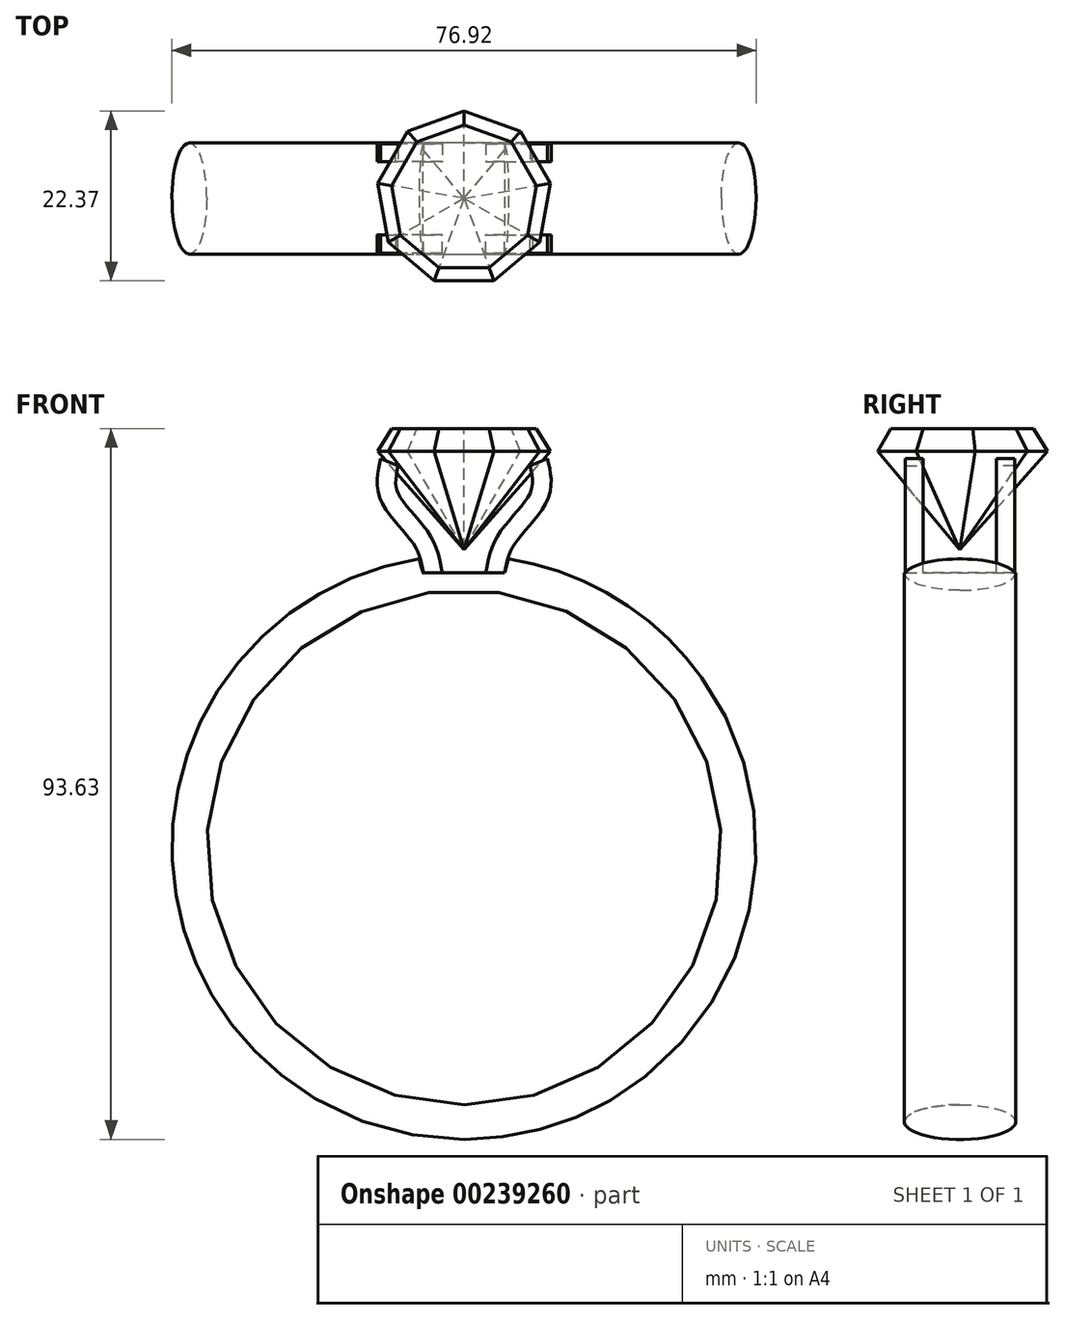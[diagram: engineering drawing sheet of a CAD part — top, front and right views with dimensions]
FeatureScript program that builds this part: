
annotation { "Feature Type Name" : "Feature", "Feature Type Description" : "" }
export const myFeature = defineFeature(function(context is Context, id is Id, definition is map)
    precondition{}
    {
        {
            var Q0;
            Q0=qCreatedBy(makeId("Right.planeOp"),FACE);
            var sketch = newSketch(context, id + "F0", { "sketchPlane" : qUnion([Q0])});
            skEllipse(sketch, "E0", {"center": v(0, 36.17) * mm, "majorRadius": 7.32 * mm, "minorRadius": 2.3 * mm, "majorAxis": v(1, 0)});
            skSolve(sketch);
        }
        {
            var Q0;
            Q0=qCreatedBy(makeId("Right.planeOp"),FACE);
            var sketch = newSketch(context, id + "F1", { "sketchPlane" : qUnion([Q0])});
            skLineSegment(sketch, "E1", {"start": v(-23.7, 0) * mm, "end": v(21.26, 0) * mm});
            skSolve(sketch);
        }
        {
            var Q0;
            Q0=makeQuery(id+"F0.imprint","IMPRINT",FACE,{"disambiguationData":[TD([[makeQuery(id+"F0.imprint","IMPRINT",EDGE,{"derivedFrom":sQuery(id+"F0.wireOp",EDGE,"E0")}),1.0]])]});
            var Q1;
            Q1=sQuery(id+"F0.wireOp",EDGE,"E0");
            var Q2;
            Q2=sQuery(id+"F1.wireOp",EDGE,"E1");
            revolve(context, id + "F2", {"entities" : qUnion([Q0]), "surfaceEntities" : qUnion([Q1]), "axis" : qUnion([Q2]), "revolveType" : RevolveType.FULL});
        }
        {
            var Q0;
            Q0=qCreatedBy(makeId("Top.planeOp"),FACE);
            var Q1;
            Q1=sQuery(id+"F0.wireOp",VERTEX,"E0.center");
            cPlane(context, id + "F3", {"entities" : qUnion([Q0, Q1]), "cplaneType" : CPlaneType.PLANE_POINT, "offset" : 100 * mm, "width" : 150 * mm, "height" : 150 * mm});
        }
        {
            var Q0;
            Q0=qCreatedBy(id+"F3.planeOp",FACE);
            var sketch = newSketch(context, id + "F4", { "sketchPlane" : qUnion([Q0])});
            skLineSegment(sketch, "E2.bottom", {"start": v(-5.43, 10.42) * mm, "end": v(5.35, 10.42) * mm});
            skLineSegment(sketch, "E2.top", {"start": v(-5.43, -11.19) * mm, "end": v(5.35, -11.19) * mm});
            skLineSegment(sketch, "E2.left", {"start": v(-5.43, 10.42) * mm, "end": v(-5.43, -11.19) * mm});
            skLineSegment(sketch, "E2.right", {"start": v(5.35, 10.42) * mm, "end": v(5.35, -11.19) * mm});
            skSolve(sketch);
        }
        {
            var Q0;
            Q0 = qSketchRegion(id + "F4", true);
            extrude(context, id + "F5", {"entities" : qUnion([Q0]), "operationType" : NewBodyOperationType.REMOVE, "depth" : 5.6 * mm, "hasDraft" : true, "draftAngle" : 15 * degree});
        }
        {
            var Q0;
            Q0=qCreatedBy(id+"F3.planeOp",FACE);
            cPlane(context, id + "F6", {"entities" : qUnion([Q0]), "cplaneType" : CPlaneType.OFFSET, "offset" : 19 * mm, "width" : 150 * mm, "height" : 150 * mm});
        }
        {
            var Q0;
            Q0=qCreatedBy(id+"F6.planeOp",FACE);
            var sketch = newSketch(context, id + "F7", { "sketchPlane" : qUnion([Q0])});
            skCircle(sketch, "E3.cCircle", {"center": v(0, 0) * mm, "radius": 9.1 * mm, "construction": true});
            skLineSegment(sketch, "E3.0", {"start": v(3.31, -9.1) * mm, "end": v(-3.31, -9.1) * mm});
            skLineSegment(sketch, "E3.1", {"start": v(-3.31, -9.1) * mm, "end": v(-8.4, -4.84) * mm});
            skLineSegment(sketch, "E3.2", {"start": v(-8.4, -4.84) * mm, "end": v(-9.54, 1.68) * mm});
            skLineSegment(sketch, "E3.3", {"start": v(-9.54, 1.68) * mm, "end": v(-6.23, 7.42) * mm});
            skLineSegment(sketch, "E3.4", {"start": v(-6.23, 7.42) * mm, "end": v(0, 9.69) * mm});
            skLineSegment(sketch, "E3.5", {"start": v(0, 9.69) * mm, "end": v(6.23, 7.42) * mm});
            skLineSegment(sketch, "E3.6", {"start": v(6.23, 7.42) * mm, "end": v(9.54, 1.68) * mm});
            skLineSegment(sketch, "E3.7", {"start": v(9.54, 1.68) * mm, "end": v(8.4, -4.84) * mm});
            skLineSegment(sketch, "E3.8", {"start": v(8.4, -4.84) * mm, "end": v(3.31, -9.1) * mm});
            skPoint(sketch, "E3.0.midPoint", {"position": v(0, -9.1) * mm});
            skSolve(sketch);
        }
        {
            var Q0;
            Q0 = qSketchRegion(id + "F7", true);
            extrude(context, id + "F8", {"entities" : qUnion([Q0]), "oppositeDirection" : true, "depth" : 3 * mm, "hasDraft" : true, "draftAngle" : 30 * degree});
        }
        {
            var Q0;
            Q0=makeQuery(id+"F8.opExtrude","CAP_FACE",FACE,{"disambiguationData":[OSD([sQuery(id+"F7.wireOp",EDGE,"E3.0"),sQuery(id+"F7.wireOp",EDGE,"E3.1"),sQuery(id+"F7.wireOp",EDGE,"E3.2"),sQuery(id+"F7.wireOp",EDGE,"E3.3"),sQuery(id+"F7.wireOp",EDGE,"E3.4"),sQuery(id+"F7.wireOp",EDGE,"E3.5"),sQuery(id+"F7.wireOp",EDGE,"E3.6"),sQuery(id+"F7.wireOp",EDGE,"E3.7"),sQuery(id+"F7.wireOp",EDGE,"E3.8")])],"isStart":false});
            extrude(context, id + "F9", {"entities" : qUnion([Q0]), "operationType" : NewBodyOperationType.ADD, "depth" : 21.3 * mm, "hasDraft" : true, "draftAngle" : 40 * degree, "draftPullDirection" : true});
        }
        {
            var Q0;
            Q0=makeQuery(id+"F5.boolean.opBoolean","COPY",FACE,{"derivedFrom":makeQuery(id+"F5.opExtrude","CAP_FACE",FACE,{"disambiguationData":[OSD([sQuery(id+"F4.wireOp",EDGE,"E2.bottom"),sQuery(id+"F4.wireOp",EDGE,"E2.top"),sQuery(id+"F4.wireOp",EDGE,"E2.left"),sQuery(id+"F4.wireOp",EDGE,"E2.right")])],"isStart":true})});
            var sketch = newSketch(context, id + "F10", { "sketchPlane" : qUnion([Q0])});
            skLineSegment(sketch, "E4.MirrorCS", {"start": v(-5.35, -7.2) * mm, "end": v(-5.35, -4.83) * mm});
            skLineSegment(sketch, "E5.MirrorCS", {"start": v(-5.35, -7.2) * mm, "end": v(-2.86, -7.2) * mm});
            skLineSegment(sketch, "E6.MirrorCS", {"start": v(-5.35, -4.83) * mm, "end": v(-2.86, -4.83) * mm});
            skLineSegment(sketch, "E7.MirrorCS", {"start": v(-2.86, -7.2) * mm, "end": v(-2.86, -4.83) * mm});
            skSolve(sketch);
        }
        {
            var Q0;
            Q0=qCreatedBy(makeId("Front.planeOp"),FACE);
            var sketch = newSketch(context, id + "F11", { "sketchPlane" : qUnion([Q0])});
            skPoint(sketch, "E8.0", {"position": v(-4.1, 36.17) * mm});
            skFitSpline(sketch, "E9", {"points": [v(-4.1, 36.17) * mm, v(-5.6, 40.6) * mm, v(-9.9, 46.36) * mm, v(-9.83, 50.78) * mm], "startDerivative": vector(-2.5, 14.05) * mm, "endDerivative": vector(3.34, 14.49) * mm});
            skSolve(sketch);
        }
        {
            var Q0;
            Q0=makeQuery(id+"F10.imprint","IMPRINT",FACE,{"disambiguationData":[TD([[makeQuery(id+"F10.imprint","IMPRINT",EDGE,{"derivedFrom":sQuery(id+"F10.wireOp",EDGE,"E4.MirrorCS")}),-1.0]])]});
            var Q1;
            Q1=sQuery(id+"F11.wireOp",EDGE,"E9");
            sweep(context, id + "F12", {"profiles" : qUnion([Q0]), "path" : qUnion([Q1])});
        }
        {
            var Q0;
            Q0=makeQuery(id+"F12.opSweep","SWEPT_BODY",BODY,{"disambiguationData":[OSD([sQuery(id+"F10.wireOp",EDGE,"E4.MirrorCS"),sQuery(id+"F10.wireOp",EDGE,"E5.MirrorCS"),sQuery(id+"F10.wireOp",EDGE,"E6.MirrorCS"),sQuery(id+"F10.wireOp",EDGE,"E7.MirrorCS"),sQuery(id+"F11.wireOp",EDGE,"E9")])]});
            var Q1;
            Q1=qCreatedBy(makeId("Right.planeOp"),FACE);
            mirror(context, id + "F13", {"entities" : qUnion([Q0]), "mirrorPlane" : qUnion([Q1])});
        }
        {
            var Q0;
            Q0=makeQuery(id+"F12.opSweep","SWEPT_BODY",BODY,{"disambiguationData":[OSD([sQuery(id+"F10.wireOp",EDGE,"E4.MirrorCS"),sQuery(id+"F10.wireOp",EDGE,"E5.MirrorCS"),sQuery(id+"F10.wireOp",EDGE,"E6.MirrorCS"),sQuery(id+"F10.wireOp",EDGE,"E7.MirrorCS"),sQuery(id+"F11.wireOp",EDGE,"E9")])]});
            var Q1;
            Q1=makeQuery(id+"F13.opPattern","COPY",BODY,{"derivedFrom":makeQuery(id+"F12.opSweep","SWEPT_BODY",BODY,{"disambiguationData":[OSD([sQuery(id+"F10.wireOp",EDGE,"E4.MirrorCS"),sQuery(id+"F10.wireOp",EDGE,"E5.MirrorCS"),sQuery(id+"F10.wireOp",EDGE,"E6.MirrorCS"),sQuery(id+"F10.wireOp",EDGE,"E7.MirrorCS"),sQuery(id+"F11.wireOp",EDGE,"E9")])]}),"instanceName":"1"});
            var Q2;
            Q2=qCreatedBy(makeId("Front.planeOp"),FACE);
            mirror(context, id + "F14", {"operationType" : NewBodyOperationType.ADD, "entities" : qUnion([Q0, Q1]), "mirrorPlane" : qUnion([Q2])});
        }
    });
